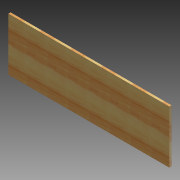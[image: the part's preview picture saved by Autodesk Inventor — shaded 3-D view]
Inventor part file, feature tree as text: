
AUTODESK INVENTOR PART (.ipt)
format: ipt  version: 2012 (Build 160160000, 160)  size: 84,992 bytes
history: native  units: in
note: dims shown in document units (in); Inventor stores cm internally (conversion verified against a paired STEP export)
features: extrude x1, sketch x1
ambient origin geometry x8: Origin, YZ Plane, XZ Plane, XY Plane, X Axis, Y Axis, Z Axis, Center Point
bodies: Solid1 (feature_tree)
feature tree (2):
  extrude  "Extrusion1"  Depth=9.0in
  sketch  "Sketch1"  dims[d0=27.375in d1=9.0in d2=0.375in d3=0.0in]
